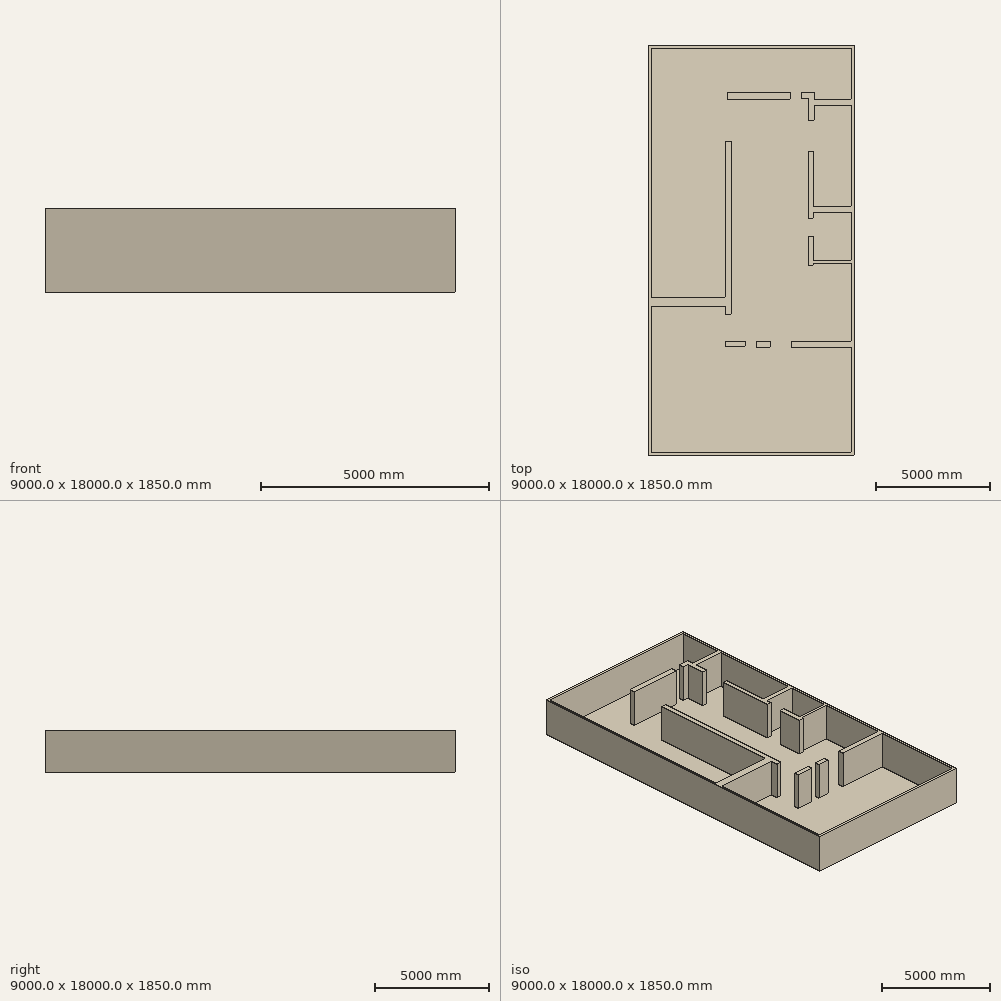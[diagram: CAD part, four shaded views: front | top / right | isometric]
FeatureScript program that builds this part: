
annotation { "Feature Type Name" : "Feature", "Feature Type Description" : "" }
export const myFeature = defineFeature(function(context is Context, id is Id, definition is map)
    precondition{}
    {
        {
            var Q0;
            Q0=qCreatedBy(makeId("Top.planeOp"),FACE);
            var sketch = newSketch(context, id + "F0", { "sketchPlane" : qUnion([Q0])});
            skLineSegment(sketch, "E0.bottom", {"start": v(0, 0) * mm, "end": v(-9000, 0) * mm});
            skLineSegment(sketch, "E0.top", {"start": v(0, 18000) * mm, "end": v(-9000, 18000) * mm});
            skLineSegment(sketch, "E0.left", {"start": v(0, 0) * mm, "end": v(0, 18000) * mm});
            skLineSegment(sketch, "E0.right", {"start": v(-9000, 0) * mm, "end": v(-9000, 18000) * mm});
            skSolve(sketch);
        }
        {
            var Q0;
            Q0 = qSketchRegion(id + "F0", true);
            extrude(context, id + "F1", {"entities" : qUnion([Q0]), "oppositeDirection" : true, "depth" : 50 * mm, "offsetDistance" : 25 * mm});
        }
        {
            var Q0;
            Q0=qCreatedBy(makeId("Top.planeOp"),FACE);
            var sketch = newSketch(context, id + "F2", { "sketchPlane" : qUnion([Q0])});
            skLineSegment(sketch, "E1.0", {"start": v(-9000, 0) * mm, "end": v(-9000, 18000) * mm});
            skLineSegment(sketch, "E2.0", {"start": v(0, 18000) * mm, "end": v(-9000, 18000) * mm});
            skLineSegment(sketch, "E3.0", {"start": v(0, 0) * mm, "end": v(0, 18000) * mm});
            skLineSegment(sketch, "E4.0", {"start": v(0, 0) * mm, "end": v(-9000, 0) * mm});
            skLineSegment(sketch, "E5.0", {"start": v(-8880.4, 119.6) * mm, "end": v(-8880.4, 17880.4) * mm});
            skLineSegment(sketch, "E5.1", {"start": v(-119.6, 119.6) * mm, "end": v(-8880.4, 119.6) * mm});
            skLineSegment(sketch, "E5.2", {"start": v(-119.6, 119.6) * mm, "end": v(-119.6, 17880.4) * mm});
            skLineSegment(sketch, "E5.3", {"start": v(-119.6, 17880.4) * mm, "end": v(-8880.4, 17880.4) * mm});
            skLineSegment(sketch, "E6.bottom", {"start": v(-3447.9, 119.6) * mm, "end": v(-3685.73, 119.6) * mm});
            skLineSegment(sketch, "E6.top", {"start": v(-3447.9, 5018.44) * mm, "end": v(-3685.73, 5018.44) * mm});
            skLineSegment(sketch, "E6.left", {"start": v(-3447.9, 119.6) * mm, "end": v(-3447.9, 5018.44) * mm});
            skLineSegment(sketch, "E6.right", {"start": v(-3685.73, 119.6) * mm, "end": v(-3685.73, 5018.44) * mm});
            skLineSegment(sketch, "E7.bottom", {"start": v(-3685.73, 5018.44) * mm, "end": v(-4277.62, 5018.44) * mm});
            skLineSegment(sketch, "E7.top", {"start": v(-3685.73, 4758.87) * mm, "end": v(-4277.62, 4758.87) * mm});
            skLineSegment(sketch, "E7.left", {"start": v(-3685.73, 5018.44) * mm, "end": v(-3685.73, 4758.87) * mm});
            skLineSegment(sketch, "E7.right", {"start": v(-4277.62, 5018.44) * mm, "end": v(-4277.62, 4758.87) * mm});
            skLineSegment(sketch, "E8.bottom", {"start": v(-2746.32, 5018.44) * mm, "end": v(-119.6, 5018.44) * mm});
            skLineSegment(sketch, "E8.top", {"start": v(-2746.32, 4723.2) * mm, "end": v(-119.6, 4723.2) * mm});
            skLineSegment(sketch, "E8.left", {"start": v(-2746.32, 5018.44) * mm, "end": v(-2746.32, 4723.2) * mm});
            skLineSegment(sketch, "E8.right", {"start": v(-119.6, 5018.44) * mm, "end": v(-119.6, 4723.2) * mm});
            skLineSegment(sketch, "E9.bottom", {"start": v(-2009.05, 5018.44) * mm, "end": v(-1771.23, 5018.44) * mm});
            skLineSegment(sketch, "E9.top", {"start": v(-2009.05, 7232.26) * mm, "end": v(-1771.23, 7232.26) * mm});
            skLineSegment(sketch, "E9.left", {"start": v(-2009.05, 5018.44) * mm, "end": v(-2009.05, 7232.26) * mm});
            skLineSegment(sketch, "E9.right", {"start": v(-1771.23, 5018.44) * mm, "end": v(-1771.23, 7232.26) * mm});
            skLineSegment(sketch, "E10.bottom", {"start": v(-2009.05, 8326.27) * mm, "end": v(-1759.33, 8326.27) * mm});
            skLineSegment(sketch, "E10.top", {"start": v(-2009.05, 9610.53) * mm, "end": v(-1759.33, 9610.53) * mm});
            skLineSegment(sketch, "E10.left", {"start": v(-2009.05, 8326.27) * mm, "end": v(-2009.05, 9610.53) * mm});
            skLineSegment(sketch, "E10.right", {"start": v(-1759.33, 8326.27) * mm, "end": v(-1759.33, 9610.53) * mm});
            skLineSegment(sketch, "E11.bottom", {"start": v(-2009.05, 10419.14) * mm, "end": v(-1771.23, 10419.14) * mm});
            skLineSegment(sketch, "E11.top", {"start": v(-2009.05, 13344.4) * mm, "end": v(-1771.23, 13344.4) * mm});
            skLineSegment(sketch, "E11.left", {"start": v(-2009.05, 10419.14) * mm, "end": v(-2009.05, 13344.4) * mm});
            skLineSegment(sketch, "E11.right", {"start": v(-1771.23, 10419.14) * mm, "end": v(-1771.23, 13344.4) * mm});
            skLineSegment(sketch, "E12.bottom", {"start": v(-2009.05, 14688.13) * mm, "end": v(-1747.44, 14688.13) * mm});
            skLineSegment(sketch, "E12.top", {"start": v(-2009.05, 15924.83) * mm, "end": v(-1747.44, 15924.83) * mm});
            skLineSegment(sketch, "E12.left", {"start": v(-2009.05, 14688.13) * mm, "end": v(-2009.05, 15924.83) * mm});
            skLineSegment(sketch, "E12.right", {"start": v(-1747.44, 14688.13) * mm, "end": v(-1747.44, 15924.83) * mm});
            skLineSegment(sketch, "E13.bottom", {"start": v(-2009.05, 15924.83) * mm, "end": v(-2294.44, 15924.83) * mm});
            skLineSegment(sketch, "E13.top", {"start": v(-2009.05, 15663.22) * mm, "end": v(-2294.44, 15663.22) * mm});
            skLineSegment(sketch, "E13.left", {"start": v(-2009.05, 15924.83) * mm, "end": v(-2009.05, 15663.22) * mm});
            skLineSegment(sketch, "E13.right", {"start": v(-2294.44, 15924.83) * mm, "end": v(-2294.44, 15663.22) * mm});
            skLineSegment(sketch, "E14.bottom", {"start": v(-2793.88, 15924.83) * mm, "end": v(-5564.56, 15924.83) * mm});
            skLineSegment(sketch, "E14.top", {"start": v(-2793.88, 15639.43) * mm, "end": v(-5564.56, 15639.43) * mm});
            skLineSegment(sketch, "E14.left", {"start": v(-2793.88, 15924.83) * mm, "end": v(-2793.88, 15639.43) * mm});
            skLineSegment(sketch, "E14.right", {"start": v(-5564.56, 15924.83) * mm, "end": v(-5564.56, 15639.43) * mm});
            skLineSegment(sketch, "E15.bottom", {"start": v(-4753.27, 5018.44) * mm, "end": v(-5621.34, 5018.44) * mm});
            skLineSegment(sketch, "E15.top", {"start": v(-4753.27, 4786.55) * mm, "end": v(-5621.34, 4786.55) * mm});
            skLineSegment(sketch, "E15.left", {"start": v(-4753.27, 5018.44) * mm, "end": v(-4753.27, 4786.55) * mm});
            skLineSegment(sketch, "E15.right", {"start": v(-5621.34, 5018.44) * mm, "end": v(-5621.34, 4786.55) * mm});
            skLineSegment(sketch, "E16.bottom", {"start": v(-5621.34, 4786.55) * mm, "end": v(-5356.78, 4786.55) * mm});
            skLineSegment(sketch, "E16.top", {"start": v(-5621.34, 119.6) * mm, "end": v(-5356.78, 119.6) * mm});
            skLineSegment(sketch, "E16.left", {"start": v(-5621.34, 4786.55) * mm, "end": v(-5621.34, 119.6) * mm});
            skLineSegment(sketch, "E16.right", {"start": v(-5356.78, 4786.55) * mm, "end": v(-5356.78, 119.6) * mm});
            skLineSegment(sketch, "E17.bottom", {"start": v(-5621.34, 5018.44) * mm, "end": v(-5377.44, 5018.44) * mm});
            skLineSegment(sketch, "E17.top", {"start": v(-5621.34, 5160.24) * mm, "end": v(-5377.44, 5160.24) * mm});
            skLineSegment(sketch, "E17.left", {"start": v(-5621.34, 5018.44) * mm, "end": v(-5621.34, 5160.24) * mm});
            skLineSegment(sketch, "E17.right", {"start": v(-5377.44, 5018.44) * mm, "end": v(-5377.44, 5160.24) * mm});
            skLineSegment(sketch, "E18.bottom", {"start": v(-5621.34, 6193.82) * mm, "end": v(-5365.48, 6193.82) * mm});
            skLineSegment(sketch, "E18.top", {"start": v(-5621.34, 13773.66) * mm, "end": v(-5365.48, 13773.66) * mm});
            skLineSegment(sketch, "E18.left", {"start": v(-5621.34, 6193.82) * mm, "end": v(-5621.34, 13773.66) * mm});
            skLineSegment(sketch, "E18.right", {"start": v(-5365.48, 6193.82) * mm, "end": v(-5365.48, 13773.66) * mm});
            skLineSegment(sketch, "E19.bottom", {"start": v(-5564.56, 15924.83) * mm, "end": v(-5387.15, 15924.83) * mm});
            skLineSegment(sketch, "E19.top", {"start": v(-5564.56, 17880.4) * mm, "end": v(-5387.15, 17880.4) * mm});
            skLineSegment(sketch, "E19.left", {"start": v(-5564.56, 15924.83) * mm, "end": v(-5564.56, 17880.4) * mm});
            skLineSegment(sketch, "E19.right", {"start": v(-5387.15, 15924.83) * mm, "end": v(-5387.15, 17880.4) * mm});
            skLineSegment(sketch, "E20.bottom", {"start": v(-5621.34, 6551.88) * mm, "end": v(-8880.4, 6551.88) * mm});
            skLineSegment(sketch, "E20.top", {"start": v(-5621.34, 6958.02) * mm, "end": v(-8880.4, 6958.02) * mm});
            skLineSegment(sketch, "E20.left", {"start": v(-5621.34, 6551.88) * mm, "end": v(-5621.34, 6958.02) * mm});
            skLineSegment(sketch, "E20.right", {"start": v(-8880.4, 6551.88) * mm, "end": v(-8880.4, 6958.02) * mm});
            skLineSegment(sketch, "E21.bottom", {"start": v(-1759.33, 8434.77) * mm, "end": v(-119.6, 8434.77) * mm});
            skLineSegment(sketch, "E21.top", {"start": v(-1759.33, 8574.76) * mm, "end": v(-119.6, 8574.76) * mm});
            skLineSegment(sketch, "E21.left", {"start": v(-1759.33, 8434.77) * mm, "end": v(-1759.33, 8574.76) * mm});
            skLineSegment(sketch, "E21.right", {"start": v(-119.6, 8434.77) * mm, "end": v(-119.6, 8574.76) * mm});
            skLineSegment(sketch, "E22.bottom", {"start": v(-1771.23, 10685.64) * mm, "end": v(-119.6, 10685.64) * mm});
            skLineSegment(sketch, "E22.top", {"start": v(-1771.23, 10916.88) * mm, "end": v(-119.6, 10916.88) * mm});
            skLineSegment(sketch, "E22.left", {"start": v(-1771.23, 10685.64) * mm, "end": v(-1771.23, 10916.88) * mm});
            skLineSegment(sketch, "E22.right", {"start": v(-119.6, 10685.64) * mm, "end": v(-119.6, 10916.88) * mm});
            skLineSegment(sketch, "E23.bottom", {"start": v(-1747.44, 15611.59) * mm, "end": v(-119.6, 15611.59) * mm});
            skLineSegment(sketch, "E23.top", {"start": v(-1747.44, 15385.33) * mm, "end": v(-119.6, 15385.33) * mm});
            skLineSegment(sketch, "E23.left", {"start": v(-1747.44, 15611.59) * mm, "end": v(-1747.44, 15385.33) * mm});
            skLineSegment(sketch, "E23.right", {"start": v(-119.6, 15611.59) * mm, "end": v(-119.6, 15385.33) * mm});
            skSolve(sketch);
        }
        {
            var Q0;
            Q0=makeQuery(id+"F2.imprint","IMPRINT",FACE,{"disambiguationData":[TD([[makeQuery(id+"F2.imprint","IMPRINT",EDGE,{"derivedFrom":sQuery(id+"F2.wireOp",EDGE,"E7.bottom")}),1.0]])]});
            var Q1;
            Q1=makeQuery(id+"F2.imprint","IMPRINT",FACE,{"disambiguationData":[TD([[makeQuery(id+"F2.imprint","IMPRINT",EDGE,{"derivedFrom":sQuery(id+"F2.wireOp",EDGE,"E6.bottom")}),-1.0]])]});
            var Q2;
            Q2=makeQuery(id+"F2.imprint","IMPRINT",FACE,{"disambiguationData":[TD([[makeQuery(id+"F2.imprint","IMPRINT",EDGE,{"derivedFrom":sQuery(id+"F2.wireOp",EDGE,"E15.bottom")}),1.0]])]});
            var Q3;
            Q3=makeQuery(id+"F2.imprint","IMPRINT",FACE,{"disambiguationData":[TD([[makeQuery(id+"F2.imprint","IMPRINT",EDGE,{"derivedFrom":sQuery(id+"F2.wireOp",EDGE,"E16.bottom")}),-1.0]])]});
            var Q4;
            Q4=makeQuery(id+"F2.imprint","IMPRINT",FACE,{"disambiguationData":[TD([[makeQuery(id+"F2.imprint","IMPRINT",EDGE,{"derivedFrom":sQuery(id+"F2.wireOp",EDGE,"E17.bottom")}),1.0]])]});
            var Q5;
            Q5=makeQuery(id+"F2.imprint","IMPRINT",FACE,{"disambiguationData":[TD([[makeQuery(id+"F2.imprint","IMPRINT",EDGE,{"derivedFrom":sQuery(id+"F2.wireOp",EDGE,"E20.bottom")}),-1.0]])]});
            var Q6;
            {var subQ3=sQuery(id+"F2.wireOp",EDGE,"E18.bottom");Q6=makeQuery(id+"F2.imprint","IMPRINT",FACE,{"disambiguationData":[TD([[makeQuery(id+"F2.imprint","IMPRINT",EDGE,{"derivedFrom":subQ3}),1.0]])]});}
            var Q7;
            Q7=makeQuery(id+"F2.imprint","IMPRINT",FACE,{"disambiguationData":[TD([[makeQuery(id+"F2.imprint","IMPRINT",EDGE,{"derivedFrom":sQuery(id+"F2.wireOp",EDGE,"E8.top")}),1.0]])]});
            var Q8;
            Q8=makeQuery(id+"F2.imprint","IMPRINT",FACE,{"disambiguationData":[TD([[makeQuery(id+"F2.imprint","IMPRINT",EDGE,{"derivedFrom":sQuery(id+"F2.wireOp",EDGE,"E9.bottom")}),1.0]])]});
            var Q9;
            {var subQ1=sQuery(id+"F2.wireOp",EDGE,"E10.bottom");Q9=makeQuery(id+"F2.imprint","IMPRINT",FACE,{"disambiguationData":[TD([[makeQuery(id+"F2.imprint","IMPRINT",EDGE,{"derivedFrom":subQ1}),1.0]])]});}
            var Q10;
            Q10=makeQuery(id+"F2.imprint","IMPRINT",FACE,{"disambiguationData":[TD([[makeQuery(id+"F2.imprint","IMPRINT",EDGE,{"derivedFrom":sQuery(id+"F2.wireOp",EDGE,"E21.bottom")}),1.0]])]});
            var Q11;
            {var subQ1=sQuery(id+"F2.wireOp",EDGE,"E11.bottom");Q11=makeQuery(id+"F2.imprint","IMPRINT",FACE,{"disambiguationData":[TD([[makeQuery(id+"F2.imprint","IMPRINT",EDGE,{"derivedFrom":subQ1}),1.0]])]});}
            var Q12;
            Q12=makeQuery(id+"F2.imprint","IMPRINT",FACE,{"disambiguationData":[TD([[makeQuery(id+"F2.imprint","IMPRINT",EDGE,{"derivedFrom":sQuery(id+"F2.wireOp",EDGE,"E22.bottom")}),1.0]])]});
            var Q13;
            Q13=makeQuery(id+"F2.imprint","IMPRINT",FACE,{"disambiguationData":[TD([[makeQuery(id+"F2.imprint","IMPRINT",EDGE,{"derivedFrom":sQuery(id+"F2.wireOp",EDGE,"E23.bottom")}),-1.0]])]});
            var Q14;
            {var subQ1=sQuery(id+"F2.wireOp",EDGE,"E12.bottom");Q14=makeQuery(id+"F2.imprint","IMPRINT",FACE,{"disambiguationData":[TD([[makeQuery(id+"F2.imprint","IMPRINT",EDGE,{"derivedFrom":subQ1}),1.0]])]});}
            var Q15;
            Q15=makeQuery(id+"F2.imprint","IMPRINT",FACE,{"disambiguationData":[TD([[makeQuery(id+"F2.imprint","IMPRINT",EDGE,{"derivedFrom":sQuery(id+"F2.wireOp",EDGE,"E13.bottom")}),1.0]])]});
            var Q16;
            Q16=makeQuery(id+"F2.imprint","IMPRINT",FACE,{"disambiguationData":[TD([[makeQuery(id+"F2.imprint","IMPRINT",EDGE,{"derivedFrom":sQuery(id+"F2.wireOp",EDGE,"E14.bottom")}),1.0]])]});
            var Q17;
            Q17=makeQuery(id+"F2.imprint","IMPRINT",FACE,{"disambiguationData":[TD([[makeQuery(id+"F2.imprint","IMPRINT",EDGE,{"derivedFrom":sQuery(id+"F2.wireOp",EDGE,"E19.bottom")}),1.0]])]});
            var Q18;
            Q18=makeQuery(id+"F2.imprint","IMPRINT",FACE,{"disambiguationData":[TD([[makeQuery(id+"F2.imprint","IMPRINT",EDGE,{"derivedFrom":sQuery(id+"F2.wireOp",EDGE,"E1.0")}),-1.0]])]});
            extrude(context, id + "F3", {"entities" : qUnion([Q0, Q1, Q2, Q3, Q4, Q5, Q6, Q7, Q8, Q9, Q10, Q11, Q12, Q13, Q14, Q15, Q16, Q17, Q18]), "operationType" : NewBodyOperationType.ADD, "depth" : 1800 * mm, "offsetDistance" : 25 * mm});
        }
    });
